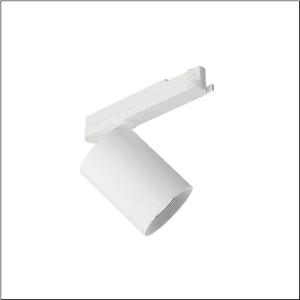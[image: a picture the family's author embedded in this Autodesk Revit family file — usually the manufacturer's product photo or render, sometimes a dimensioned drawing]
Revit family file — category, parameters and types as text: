
# Revit family: spot_11_51sd15mbd5a
name_source: partatom
category: Lighting Fixtures
units: mm (PartAtom-declared; Revit-internal decimal feet)

## family parameters
Cut with Voids When Loaded = No
Host = Face
Light Source = No
Part Type = Normal
Room Calculation Point = No
Round Connector Dimension = Use Diameter
Shared = No

## types (1)
- --- (1 x LED, 7520 lm, 50.9 W, 4000K)
    Apparent Load = 51 VA
    CIE Flux Codes = 91 98 100 100 100
    Color Rendering = 90
    Color Temperature = 4000K
    Default Elevation = 1800 mm
    Description = Spot 11, directional spotlight, light control with lens, of PMMA, LED rated luminous flux: 5.870lm, light colour: 940, control gear: ECG Multilumen, with 3-phase adapter, mains connection: 220..240V, AC, 50/60Hz, of aluminium, traffic white (RAL 9016), length: 213mm, diameter: 105mm, protection rating (complete): IP20, insulation class (complete): insulation class I (protective earthing), certification: CE, impact resistance: IK02, permissible ambient temperature for indoor applications: -20..+40°C, packaging unit: 1 piece
    Height = 175 mm
    Lamp = 1 x LED
    Lamp Light Flux = 7520 lm
    Lamp Power = 50.9 W
    Lamp count = 1
    Length = 105 mm
    Luminous efficacy = 148 lm/W
    Manufacturer = Siteco
    ModVariant = No
    Model = 51SD15MBD5A
    Mounting Place = Ceiling
    Mounting Type = Pendant
    Number of Poles = 1
    OnlyDefault = Yes
    Power Factor = 1
    Product Name = Spot 11
    Product group = directional spotlight
    ProductGroupID = 905
    Protection Class = Protection class I
    Protection Degree = IP 20
    RLX_Detail_Level = 1
    RLX_Emergency_Light_Flux = 0 lm
    RLX_Emergency_Type = 0
    RLX_Emergency_Type_DB = No
    RlxData = <blob elided: 17661 chars, md5=be2550ea>
    Socket = socket
    Standby Power = 0 W
    System Light Flux = 7520 lm
    System Power = 51 W
    Type Comments = factory setting: luminous flux: 100 % | (ON | ON | ON | ON) | 1050 mA
    Type Image = l_1006697.jpg
    URL = http://relux.com
    VarID = @adj_097095
    Voltage = 0 V
    Weight = 0.00 kg
    Width = 0 mm  [stored 0 ft]

note: [stored X ft] marks values corroborated as IEEE doubles in the binary element streams (Revit-internal decimal feet)

## geometry (parser evidence)
native form markers: Blend x4, Sweep x10
no freeform markers — native parametric forms only
